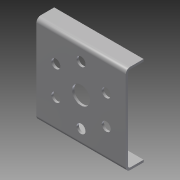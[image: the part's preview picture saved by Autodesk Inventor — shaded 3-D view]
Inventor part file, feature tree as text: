
AUTODESK INVENTOR PART (.ipt)
format: ipt  version: 2014 (Build 180170000, 170)  size: 135,680 bytes
history: native  units: in
note: dims shown in document units (in); Inventor stores cm internally (conversion verified against a paired STEP export)
features: sheet_metal_op x6, other x3, sketch x2
ambient origin geometry x8: Origin, YZ Plane, XZ Plane, XY Plane, X Axis, Y Axis, Z Axis, Center Point
bodies: Body1 (feature_tree)
feature tree (11):
  sheet_metal_op  "Face2"
  sheet_metal_op  "Face3"
  sheet_metal_op  "Flange1"
  other  "Plate2"
  sketch  "Sketch3"  dims[d0=5.0in]
  other  "Plate3"
  sheet_metal_op  "Bend1"
  sketch  "Sketch4"  dims[d1=1.0in d2=0.5in d3=1.625in d8=0.125in d19=0.125in d20=2.3622in d22=360.0deg d24=0.125in d25=0.125in d26=0.0625in d27=0.25in d28=0.125in d29=0.125in d30=0.0625in d31=0.25in d32=0.125in d33=1.0in d34=90.0deg d35=0.125in d36=0.5in d37=0.125in d38=0.125in]
  other  "Plate4"
  sheet_metal_op  "Bend2"
  sheet_metal_op  "Corner1"
